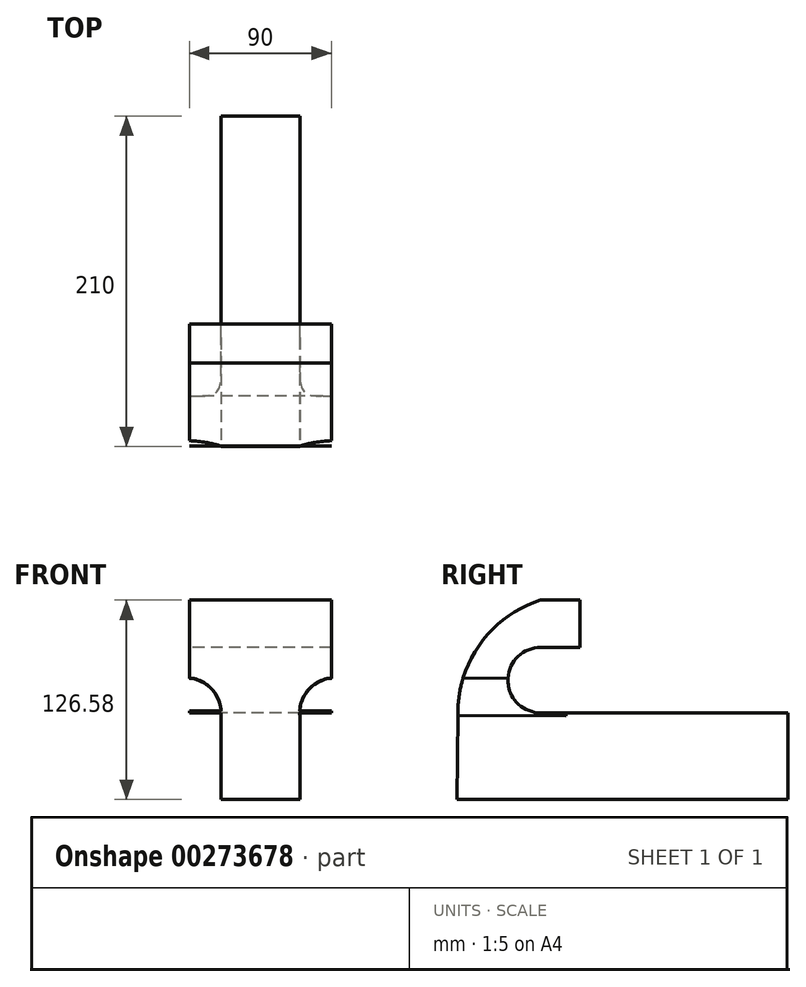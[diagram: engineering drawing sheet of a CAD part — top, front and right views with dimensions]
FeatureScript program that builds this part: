
annotation { "Feature Type Name" : "Feature", "Feature Type Description" : "" }
export const myFeature = defineFeature(function(context is Context, id is Id, definition is map)
    precondition{}
    {
        {
            var Q0;
            Q0=qCreatedBy(makeId("Right.planeOp"),FACE);
            var sketch = newSketch(context, id + "F0", { "sketchPlane" : qUnion([Q0])});
            skPoint(sketch, "E0.visualSharp", {"position": v(-127.51, 44.94) * mm});
            skArc(sketch, "E0.filletArc", {"start": v(-126.62, 46.23) * mm, "mid": v(-127.28, 44.87) * mm, "end": v(-127.51, 43.37) * mm});
            skLineSegment(sketch, "E1.bottom", {"start": v(-57.65, -14.75) * mm, "end": v(99.35, -14.75) * mm});
            skLineSegment(sketch, "E1.top", {"start": v(-110.65, -69.75) * mm, "end": v(99.35, -69.75) * mm});
            skLineSegment(sketch, "E2", {"start": v(-57.65, 26.83) * mm, "end": v(-32.65, 26.83) * mm});
            skLineSegment(sketch, "E3", {"start": v(-32.65, 26.83) * mm, "end": v(-32.65, 56.83) * mm});
            skLineSegment(sketch, "E4", {"start": v(-32.65, 56.83) * mm, "end": v(-57.65, 56.83) * mm});
            skArc(sketch, "E5", {"start": v(-57.65, 56.83) * mm, "mid": v(-95.68, 29.66) * mm, "end": v(-110.25, -14.75) * mm});
            skArc(sketch, "E6", {"start": v(-57.65, 26.83) * mm, "mid": v(-78.44, 6.04) * mm, "end": v(-57.65, -14.75) * mm});
            skLineSegment(sketch, "E7", {"start": v(-110.25, -14.75) * mm, "end": v(-110.65, -69.75) * mm});
            skLineSegment(sketch, "E8", {"start": v(99.35, -14.75) * mm, "end": v(99.35, -69.75) * mm});
            skSolve(sketch);
        }
        {
            var Q0;
            Q0 = qSketchRegion(id + "F0", true);
            extrude(context, id + "F1", {"entities" : qUnion([Q0]), "depth" : 90 * mm});
        }
        {
            var Q0;
            Q0=makeQuery(id+"F1.opExtrude","SWEPT_FACE",FACE,{"disambiguationData":[OSD([sQuery(id+"F0.wireOp",EDGE,"E8")])]});
            var sketch = newSketch(context, id + "F2", { "sketchPlane" : qUnion([Q0])});
            skLineSegment(sketch, "E9", {"start": v(-70, -14.75) * mm, "end": v(-70, -69.75) * mm});
            skLineSegment(sketch, "E10", {"start": v(-20, -14.75) * mm, "end": v(-20, -69.75) * mm});
            skSolve(sketch);
        }
        {
            var Q0;
            {var subQ0=sQuery(id+"F2.wireOp",EDGE,"E10");Q0=makeQuery(id+"F2.imprint","IMPRINT",FACE,{"disambiguationData":[TD([[makeQuery(id+"F2.imprint","IMPRINT",EDGE,{"derivedFrom":subQ0}),1.0]])]});}
            var Q1;
            {var subQ0=sQuery(id+"F2.wireOp",EDGE,"E9");Q1=makeQuery(id+"F2.imprint","IMPRINT",FACE,{"disambiguationData":[TD([[makeQuery(id+"F2.imprint","IMPRINT",EDGE,{"derivedFrom":subQ0}),-1.0]])]});}
            extrude(context, id + "F3", {"entities" : qUnion([Q0, Q1]), "operationType" : NewBodyOperationType.REMOVE, "oppositeDirection" : true, "depth" : 210 * mm});
        }
        {
            var Q0;
            Q0=makeQuery(id+"F1.opExtrude","SWEPT_FACE",FACE,{"disambiguationData":[OSD([sQuery(id+"F0.wireOp",EDGE,"E7")])]});
            var sketch = newSketch(context, id + "F4", { "sketchPlane" : qUnion([Q0])});
            skLineSegment(sketch, "E11", {"start": v(45, 58.08) * mm, "end": v(45, -70.56) * mm, "construction": true});
            skLineSegment(sketch, "E12.left", {"start": v(20, -15.56) * mm, "end": v(20, -17.1) * mm});
            skLineSegment(sketch, "E12.right", {"start": v(-2.3, -15.56) * mm, "end": v(-2.3, -17.1) * mm});
            skArc(sketch, "E13", {"start": v(20, -17.1) * mm, "mid": v(14.04, -0.3) * mm, "end": v(-2.3, 6.8) * mm});
            skLineSegment(sketch, "E14", {"start": v(-2.3, -15.56) * mm, "end": v(-2.3, 6.8) * mm});
            skLineSegment(sketch, "E15.MirrorCS", {"start": v(92.3, -15.56) * mm, "end": v(92.3, -17.1) * mm});
            skLineSegment(sketch, "E16.MirrorCS", {"start": v(92.3, -15.56) * mm, "end": v(92.3, 6.8) * mm});
            skArc(sketch, "E17.MirrorCS", {"start": v(70, -17.1) * mm, "mid": v(75.96, -0.3) * mm, "end": v(92.3, 6.8) * mm});
            skLineSegment(sketch, "E18.MirrorCS", {"start": v(70, -15.56) * mm, "end": v(70, -17.1) * mm});
            skLineSegment(sketch, "E19", {"start": v(20, -17.1) * mm, "end": v(-2.3, -17.1) * mm});
            skLineSegment(sketch, "E20", {"start": v(70, -17.1) * mm, "end": v(92.3, -17.1) * mm});
            skPoint(sketch, "E12.top.end.orphan", {"position": v(-2.3, -70.45) * mm});
            skPoint(sketch, "E21.MirrorCS.end.orphan", {"position": v(92.3, -70.45) * mm});
            skPoint(sketch, "E21.MirrorCS.start.orphan", {"position": v(70, -70.45) * mm});
            skPoint(sketch, "E22.orphan", {"position": v(20, -70.45) * mm});
            skSolve(sketch);
        }
        {
            var Q0;
            Q0 = qSketchRegion(id + "F4", true);
            extrude(context, id + "F5", {"entities" : qUnion([Q0]), "operationType" : NewBodyOperationType.REMOVE, "oppositeDirection" : true, "depth" : 68.8 * mm});
        }
    });
